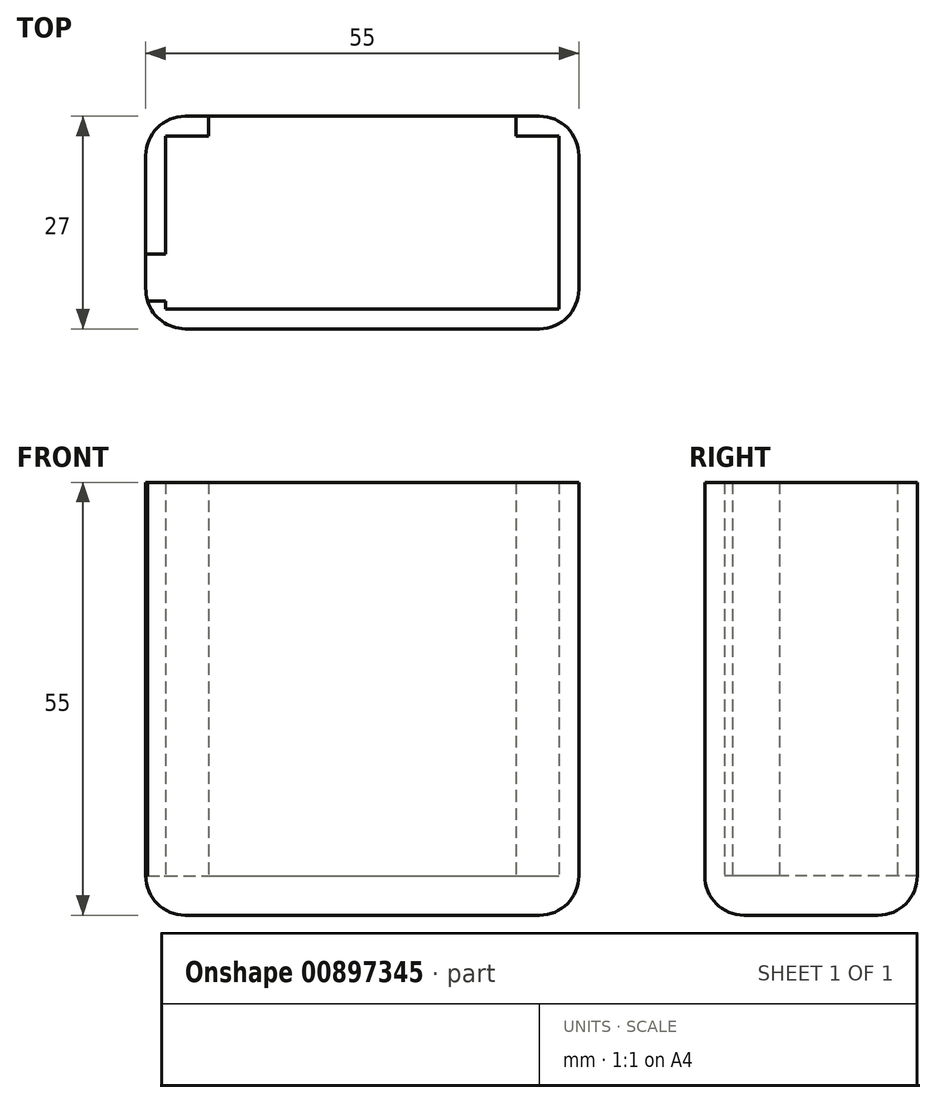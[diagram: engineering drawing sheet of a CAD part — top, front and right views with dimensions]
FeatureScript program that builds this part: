
annotation { "Feature Type Name" : "Feature", "Feature Type Description" : "" }
export const myFeature = defineFeature(function(context is Context, id is Id, definition is map)
    precondition{}
    {
        {
            var Q0;
            Q0=qCreatedBy(makeId("Top.planeOp"),FACE);
            var sketch = newSketch(context, id + "F0", { "sketchPlane" : qUnion([Q0])});
            skLineSegment(sketch, "E0.bottom", {"start": v(-27.5, 13.5) * mm, "end": v(27.5, 13.5) * mm});
            skLineSegment(sketch, "E0.top", {"start": v(-27.5, -13.5) * mm, "end": v(27.5, -13.5) * mm});
            skLineSegment(sketch, "E0.left", {"start": v(-27.5, 13.5) * mm, "end": v(-27.5, -13.5) * mm});
            skLineSegment(sketch, "E0.right", {"start": v(27.5, 13.5) * mm, "end": v(27.5, -13.5) * mm});
            skPoint(sketch, "E0.middle", {"position": v(0, 0) * mm});
            skLineSegment(sketch, "E1.bottom", {"start": v(25, -11) * mm, "end": v(-25, -11) * mm});
            skLineSegment(sketch, "E1.top", {"start": v(25, 11) * mm, "end": v(-25, 11) * mm});
            skLineSegment(sketch, "E1.left", {"start": v(25, -11) * mm, "end": v(25, 11) * mm});
            skLineSegment(sketch, "E1.right", {"start": v(-25, -11) * mm, "end": v(-25, 11) * mm});
            skLineSegment(sketch, "E2.bottom", {"start": v(19.5, 3.38) * mm, "end": v(-19.5, 3.38) * mm});
            skLineSegment(sketch, "E2.top", {"start": v(19.5, 35.6) * mm, "end": v(-19.5, 35.6) * mm});
            skLineSegment(sketch, "E2.left", {"start": v(19.5, 3.38) * mm, "end": v(19.5, 35.6) * mm});
            skLineSegment(sketch, "E2.right", {"start": v(-19.5, 3.38) * mm, "end": v(-19.5, 35.6) * mm});
            skLineSegment(sketch, "E3.bottom", {"start": v(-18.54, -10) * mm, "end": v(-48.16, -10) * mm});
            skLineSegment(sketch, "E3.top", {"start": v(-18.54, -4) * mm, "end": v(-48.16, -4) * mm});
            skLineSegment(sketch, "E3.left", {"start": v(-18.54, -10) * mm, "end": v(-18.54, -4) * mm});
            skLineSegment(sketch, "E3.right", {"start": v(-48.16, -10) * mm, "end": v(-48.16, -4) * mm});
            skSolve(sketch);
        }
        {
            var Q0;
            {var subQ1=sQuery(id+"F0.wireOp",EDGE,"E0.top");Q0=makeQuery(id+"F0.imprint","IMPRINT",FACE,{"disambiguationData":[TD([[makeQuery(id+"F0.imprint","IMPRINT",EDGE,{"derivedFrom":subQ1}),1.0]])]});}
            var Q1;
            {var subQ5=sQuery(id+"F0.wireOp",EDGE,"E0.left");var subQ6=sQuery(id+"F0.wireOp",EDGE,"E0.bottom");var subQ7=makeQuery(id+"F0.imprint","INTERSECT",VERTEX,{"derivedFrom":[subQ6,subQ5]});Q1=makeQuery(id+"F0.imprint","IMPRINT",FACE,{"disambiguationData":[TD([[makeQuery(id+"F0.imprint","IMPRINT",EDGE,{"disambiguationData":[TD([[subQ7,-1.0]])],"derivedFrom":subQ6}),-1.0]])]});}
            var Q2;
            {var subQ13=sQuery(id+"F0.wireOp",EDGE,"E1.bottom");Q2=makeQuery(id+"F0.imprint","IMPRINT",FACE,{"disambiguationData":[TD([[makeQuery(id+"F0.imprint","IMPRINT",EDGE,{"derivedFrom":subQ13}),-1.0]])]});}
            var Q3;
            {var subQ5=sQuery(id+"F0.wireOp",EDGE,"E2.bottom");Q3=makeQuery(id+"F0.imprint","IMPRINT",FACE,{"disambiguationData":[TD([[makeQuery(id+"F0.imprint","IMPRINT",EDGE,{"derivedFrom":subQ5}),-1.0]])]});}
            var Q4;
            {var subQ0=sQuery(id+"F0.wireOp",EDGE,"E2.right");var subQ1=sQuery(id+"F0.wireOp",EDGE,"E0.bottom");var subQ2=makeQuery(id+"F0.imprint","INTERSECT",VERTEX,{"derivedFrom":[subQ1,subQ0]});Q4=makeQuery(id+"F0.imprint","IMPRINT",FACE,{"disambiguationData":[TD([[makeQuery(id+"F0.imprint","IMPRINT",EDGE,{"disambiguationData":[TD([[subQ2,-1.0]])],"derivedFrom":subQ1}),-1.0]])]});}
            var Q5;
            {var subQ5=sQuery(id+"F0.wireOp",EDGE,"E3.left");Q5=makeQuery(id+"F0.imprint","IMPRINT",FACE,{"disambiguationData":[TD([[makeQuery(id+"F0.imprint","IMPRINT",EDGE,{"derivedFrom":subQ5}),1.0]])]});}
            var Q6;
            {var subQ0=sQuery(id+"F0.wireOp",EDGE,"E3.top");var subQ1=sQuery(id+"F0.wireOp",EDGE,"E0.left");var subQ2=makeQuery(id+"F0.imprint","INTERSECT",VERTEX,{"derivedFrom":[subQ1,subQ0]});Q6=makeQuery(id+"F0.imprint","IMPRINT",FACE,{"disambiguationData":[TD([[makeQuery(id+"F0.imprint","IMPRINT",EDGE,{"disambiguationData":[TD([[subQ2,-1.0]])],"derivedFrom":subQ1}),1.0]])]});}
            extrude(context, id + "F1", {"entities" : qUnion([Q0, Q1, Q2, Q3, Q4, Q5, Q6]), "depth" : 5 * mm, "offsetDistance" : 25 * mm});
        }
        {
            var Q0;
            {var subQ1=sQuery(id+"F0.wireOp",EDGE,"E0.top");Q0=makeQuery(id+"F0.imprint","IMPRINT",FACE,{"disambiguationData":[TD([[makeQuery(id+"F0.imprint","IMPRINT",EDGE,{"derivedFrom":subQ1}),1.0]])]});}
            var Q1;
            {var subQ5=sQuery(id+"F0.wireOp",EDGE,"E0.left");var subQ6=sQuery(id+"F0.wireOp",EDGE,"E0.bottom");var subQ7=makeQuery(id+"F0.imprint","INTERSECT",VERTEX,{"derivedFrom":[subQ6,subQ5]});Q1=makeQuery(id+"F0.imprint","IMPRINT",FACE,{"disambiguationData":[TD([[makeQuery(id+"F0.imprint","IMPRINT",EDGE,{"disambiguationData":[TD([[subQ7,-1.0]])],"derivedFrom":subQ6}),-1.0]])]});}
            extrude(context, id + "F2", {"entities" : qUnion([Q0, Q1]), "operationType" : NewBodyOperationType.ADD, "depth" : 55 * mm, "offsetDistance" : 25 * mm});
        }
        {
            var Q0;
            {var subQ0=sQuery(id+"F0.wireOp",EDGE,"E0.right");var subQ1=sQuery(id+"F0.wireOp",EDGE,"E0.bottom");Q0=makeQuery(id+"F2.boolean.opBoolean","MERGE",EDGE,{"derivedFrom":[makeQuery(id+"F1.opExtrude","SWEPT_EDGE",EDGE,{"disambiguationData":[OSD([subQ1,subQ0])]}),makeQuery(id+"F2.opExtrude","SWEPT_EDGE",EDGE,{"disambiguationData":[OSD([subQ1,subQ0])]})]});}
            var Q1;
            {var subQ0=sQuery(id+"F0.wireOp",EDGE,"E0.left");var subQ1=sQuery(id+"F0.wireOp",EDGE,"E0.bottom");Q1=makeQuery(id+"F2.boolean.opBoolean","MERGE",EDGE,{"derivedFrom":[makeQuery(id+"F1.opExtrude","SWEPT_EDGE",EDGE,{"disambiguationData":[OSD([subQ1,subQ0])]}),makeQuery(id+"F2.opExtrude","SWEPT_EDGE",EDGE,{"disambiguationData":[OSD([subQ1,subQ0])]})]});}
            var Q2;
            {var subQ0=sQuery(id+"F0.wireOp",EDGE,"E0.left");var subQ1=sQuery(id+"F0.wireOp",EDGE,"E0.top");Q2=makeQuery(id+"F2.boolean.opBoolean","MERGE",EDGE,{"derivedFrom":[makeQuery(id+"F1.opExtrude","SWEPT_EDGE",EDGE,{"disambiguationData":[OSD([subQ1,subQ0])]}),makeQuery(id+"F2.opExtrude","SWEPT_EDGE",EDGE,{"disambiguationData":[OSD([subQ1,subQ0])]})]});}
            var Q3;
            {var subQ0=sQuery(id+"F0.wireOp",EDGE,"E0.right");var subQ1=sQuery(id+"F0.wireOp",EDGE,"E0.top");Q3=makeQuery(id+"F2.boolean.opBoolean","MERGE",EDGE,{"derivedFrom":[makeQuery(id+"F1.opExtrude","SWEPT_EDGE",EDGE,{"disambiguationData":[OSD([subQ1,subQ0])]}),makeQuery(id+"F2.opExtrude","SWEPT_EDGE",EDGE,{"disambiguationData":[OSD([subQ1,subQ0])]})]});}
            var Q4;
            Q4=makeQuery(id+"F1.opExtrude","CAP_EDGE",EDGE,{"disambiguationData":[OSD([sQuery(id+"F0.wireOp",EDGE,"E0.left")])],"isStart":true});
            var Q5;
            Q5=makeQuery(id+"F1.opExtrude","CAP_EDGE",EDGE,{"disambiguationData":[OSD([sQuery(id+"F0.wireOp",EDGE,"E0.bottom")])],"isStart":true});
            var Q6;
            Q6=makeQuery(id+"F1.opExtrude","CAP_EDGE",EDGE,{"disambiguationData":[OSD([sQuery(id+"F0.wireOp",EDGE,"E0.right")])],"isStart":true});
            var Q7;
            Q7=makeQuery(id+"F1.opExtrude","CAP_EDGE",EDGE,{"disambiguationData":[OSD([sQuery(id+"F0.wireOp",EDGE,"E0.top")])],"isStart":true});
            fillet(context, id + "F3", {"entities" : qUnion([Q0, Q1, Q2, Q3, Q4, Q5, Q6, Q7]), "radius" : 5 * mm, "tangentPropagation" : true, "allowEdgeOverflow" : false});
        }
    });
